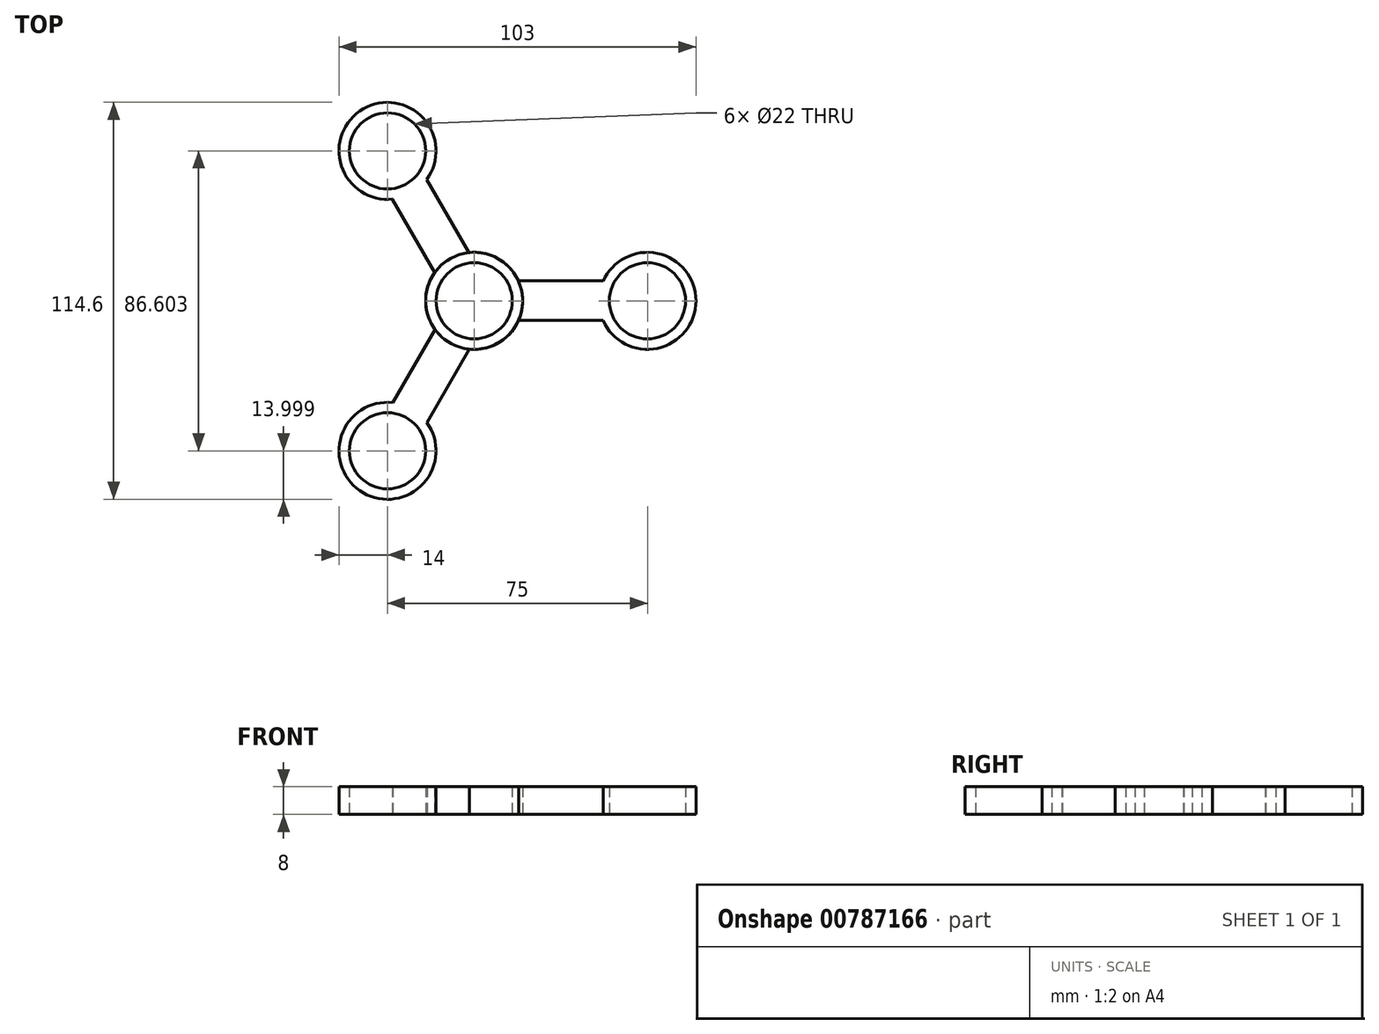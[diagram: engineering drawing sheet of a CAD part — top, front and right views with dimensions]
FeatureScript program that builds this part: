
annotation { "Feature Type Name" : "Feature", "Feature Type Description" : "" }
export const myFeature = defineFeature(function(context is Context, id is Id, definition is map)
    precondition{}
    {
        {
            var Q0;
            Q0=qCreatedBy(makeId("Top.planeOp"),FACE);
            var sketch = newSketch(context, id + "F0", { "sketchPlane" : qUnion([Q0])});
            skCircle(sketch, "E0", {"center": v(0, 0) * mm, "radius": 14 * mm});
            skCircle(sketch, "E1", {"center": v(0, 0) * mm, "radius": 11 * mm});
            skCircle(sketch, "E2", {"center": v(50, 0) * mm, "radius": 14 * mm});
            skCircle(sketch, "E3", {"center": v(50, 0) * mm, "radius": 11 * mm});
            skLineSegment(sketch, "E4.bottom", {"start": v(12.76, 5.77) * mm, "end": v(37.2, 5.77) * mm});
            skLineSegment(sketch, "E4.top", {"start": v(12.76, -5.65) * mm, "end": v(37.2, -5.65) * mm});
            skLineSegment(sketch, "E4.right", {"start": v(37.2, 5.77) * mm, "end": v(37.2, 5.65) * mm});
            skSolve(sketch);
        }
        {
            var Q0;
            {var subQ6=sQuery(id+"F0.wireOp",EDGE,"E4.bottom");Q0=makeQuery(id+"F0.imprint","IMPRINT",FACE,{"disambiguationData":[TD([[makeQuery(id+"F0.imprint","IMPRINT",EDGE,{"derivedFrom":subQ6}),-1.0]])]});}
            var Q1;
            Q1=makeQuery(id+"F0.imprint","IMPRINT",FACE,{"disambiguationData":[TD([[makeQuery(id+"F0.imprint","IMPRINT",EDGE,{"derivedFrom":sQuery(id+"F0.wireOp",EDGE,"E1")}),-1.0]])]});
            var Q2;
            Q2=makeQuery(id+"F0.imprint","IMPRINT",FACE,{"disambiguationData":[TD([[makeQuery(id+"F0.imprint","IMPRINT",EDGE,{"derivedFrom":sQuery(id+"F0.wireOp",EDGE,"E3")}),-1.0]])]});
            extrude(context, id + "F1", {"entities" : qUnion([Q0, Q1, Q2]), "depth" : 8 * mm, "offsetDistance" : 25 * mm});
        }
        {
            var Q0;
            Q0=qCreatedBy(makeId("Front.planeOp"),FACE);
            var sketch = newSketch(context, id + "F2", { "sketchPlane" : qUnion([Q0])});
            skLineSegment(sketch, "E5", {"start": v(0, 0) * mm, "end": v(0, 68.76) * mm, "construction": true});
            skSolve(sketch);
        }
        {
            var Q0;
            Q0=makeQuery(id+"F1.opExtrude","SWEPT_BODY",BODY,{"disambiguationData":[OSD([sQuery(id+"F0.wireOp",EDGE,"E0"),sQuery(id+"F0.wireOp",EDGE,"E1"),sQuery(id+"F0.wireOp",EDGE,"E2"),sQuery(id+"F0.wireOp",EDGE,"E3"),sQuery(id+"F0.wireOp",EDGE,"E4.bottom"),sQuery(id+"F0.wireOp",EDGE,"E4.top"),sQuery(id+"F0.wireOp",EDGE,"E4.right")])]});
            var Q1;
            Q1=sQuery(id+"F2.wireOp",EDGE,"E5");
            circularPattern(context, id + "F3", {"entities" : qUnion([Q0]), "axis" : qUnion([Q1]), "angle" : 360 * degree, "instanceCount" : 3, "equalSpace" : true});
        }
    });
